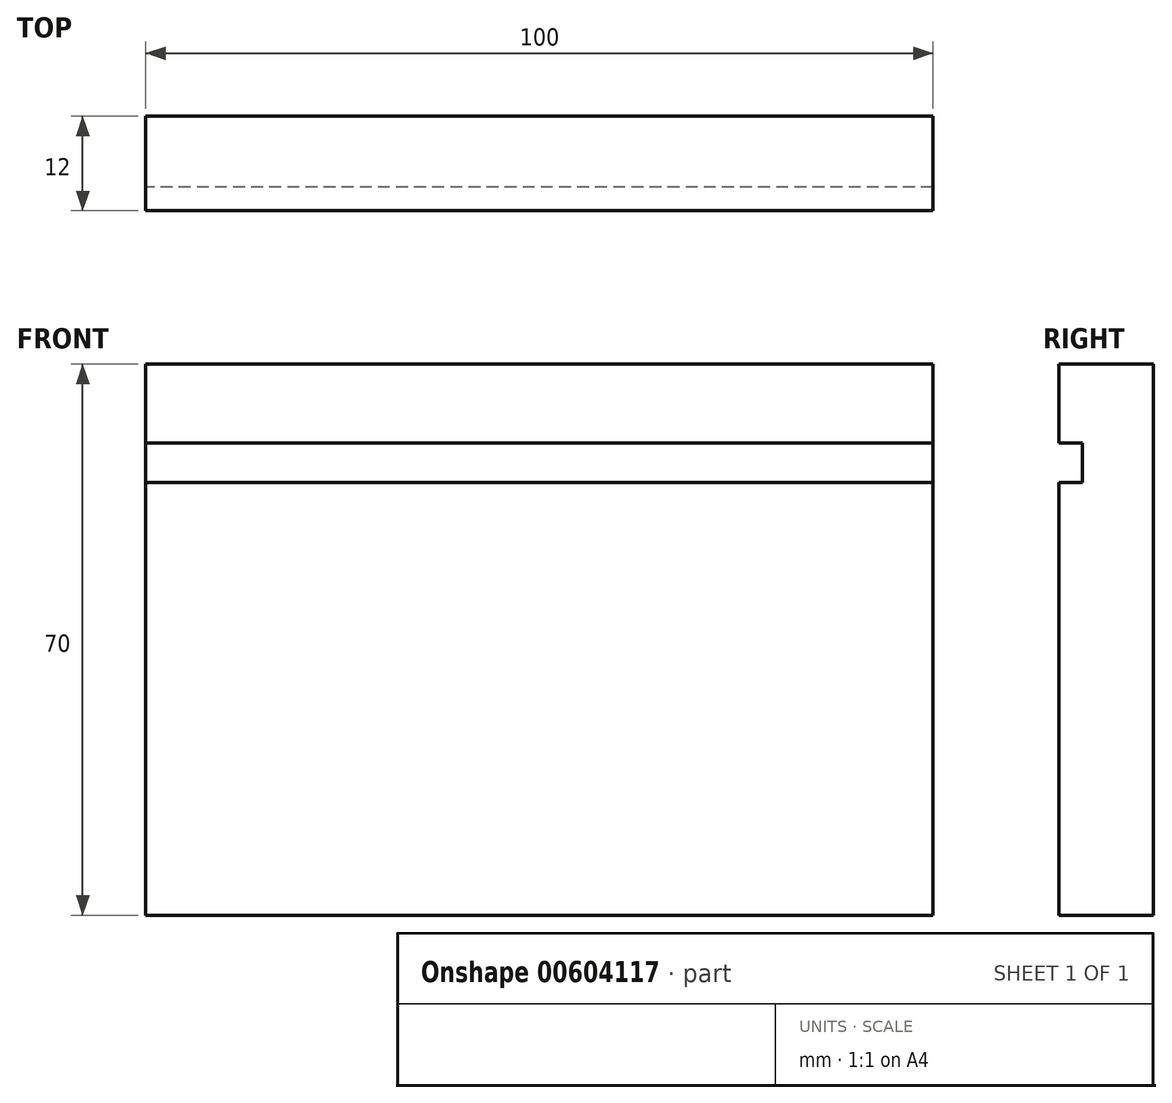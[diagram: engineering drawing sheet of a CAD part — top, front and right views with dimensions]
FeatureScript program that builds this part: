
annotation { "Feature Type Name" : "Feature", "Feature Type Description" : "" }
export const myFeature = defineFeature(function(context is Context, id is Id, definition is map)
    precondition{}
    {
        {
            var Q0;
            Q0=qCreatedBy(makeId("Right.planeOp"),FACE);
            var sketch = newSketch(context, id + "F0", { "sketchPlane" : qUnion([Q0])});
            skLineSegment(sketch, "E0", {"start": v(0, 0) * mm, "end": v(0, 70) * mm});
            skLineSegment(sketch, "E1", {"start": v(0, 70) * mm, "end": v(-12, 70) * mm});
            skLineSegment(sketch, "E2", {"start": v(-12, 70) * mm, "end": v(-12, 60) * mm});
            skLineSegment(sketch, "E3", {"start": v(-12, 60) * mm, "end": v(-9, 60) * mm});
            skLineSegment(sketch, "E4", {"start": v(-9, 60) * mm, "end": v(-9, 55) * mm});
            skLineSegment(sketch, "E5", {"start": v(-9, 55) * mm, "end": v(-12, 55) * mm});
            skLineSegment(sketch, "E6", {"start": v(-12, 55) * mm, "end": v(-12, 0) * mm});
            skLineSegment(sketch, "E7", {"start": v(-12, 0) * mm, "end": v(0, 0) * mm});
            skSolve(sketch);
        }
        {
            var Q0;
            Q0 = qSketchRegion(id + "F0", true);
            extrude(context, id + "F1", {"entities" : qUnion([Q0]), "depth" : 100 * mm, "offsetDistance" : 25 * mm});
        }
    });
